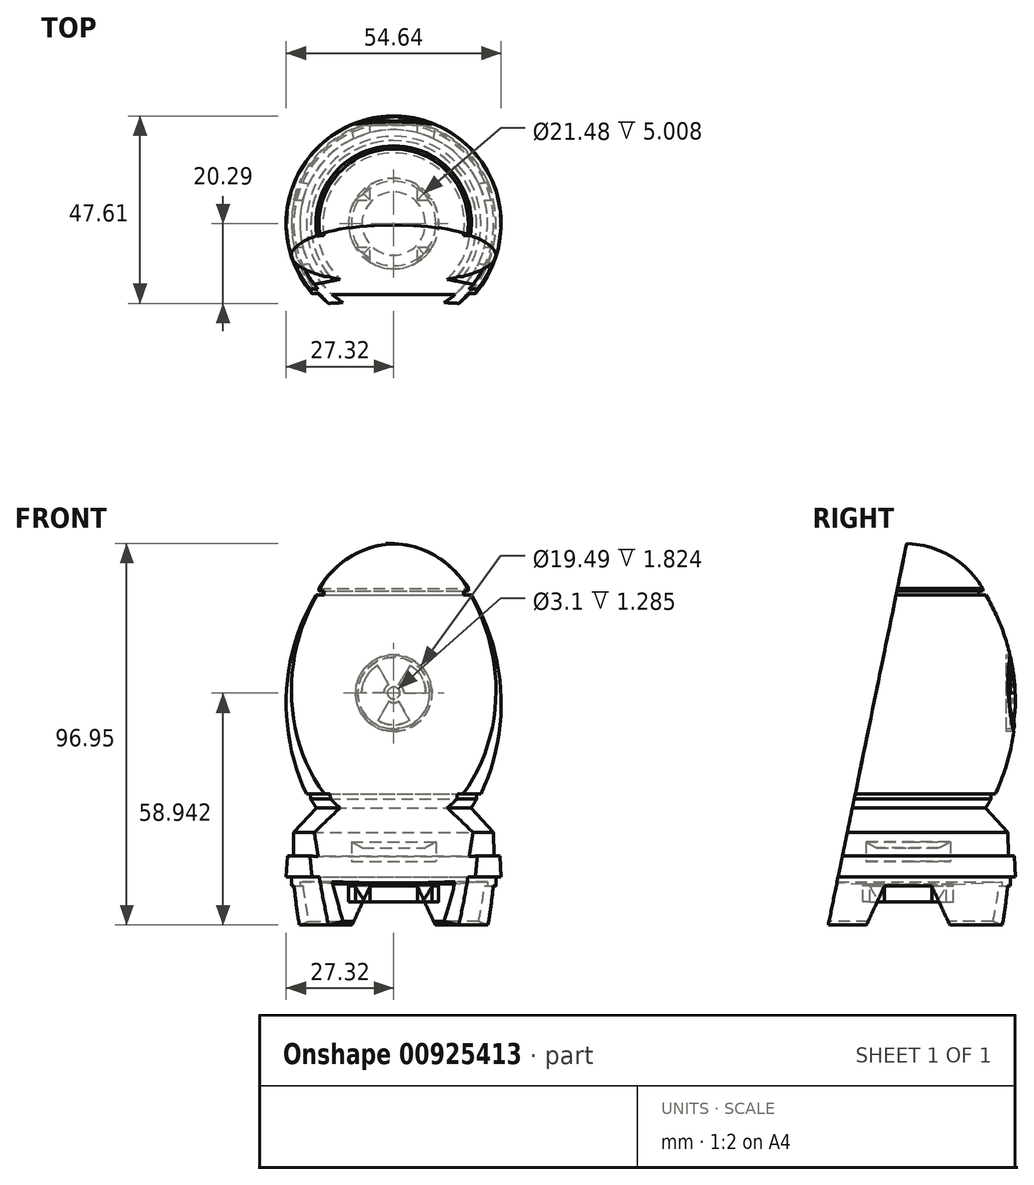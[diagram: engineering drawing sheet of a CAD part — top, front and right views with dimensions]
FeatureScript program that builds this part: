
annotation { "Feature Type Name" : "Feature", "Feature Type Description" : "" }
export const myFeature = defineFeature(function(context is Context, id is Id, definition is map)
    precondition{}
    {
        {
            var Q0;
            Q0=qCreatedBy(makeId("Front.planeOp"),FACE);
            var sketch = newSketch(context, id + "F0", { "sketchPlane" : qUnion([Q0])});
            skLineSegment(sketch, "E0", {"start": v(0, 0) * mm, "end": v(0, 100) * mm, "construction": true});
            skArc(sketch, "E1", {"start": v(18.96, 88.63) * mm, "mid": v(10.92, 96.72) * mm, "end": v(0, 100) * mm});
            skLineSegment(sketch, "E2", {"start": v(18.96, 88.63) * mm, "end": v(18.96, 87.9) * mm});
            skLineSegment(sketch, "E3", {"start": v(18.96, 87.9) * mm, "end": v(17.96, 87.9) * mm});
            skLineSegment(sketch, "E4", {"start": v(17.96, 87.9) * mm, "end": v(17.96, 86.91) * mm});
            skLineSegment(sketch, "E5", {"start": v(17.96, 86.91) * mm, "end": v(19.76, 86.91) * mm});
            skArc(sketch, "E6", {"start": v(22.17, 36.4) * mm, "mid": v(27.23, 61.96) * mm, "end": v(19.76, 86.91) * mm});
            skLineSegment(sketch, "E7", {"start": v(22.17, 36.4) * mm, "end": v(21.07, 36.4) * mm});
            skLineSegment(sketch, "E8", {"start": v(21.07, 36.4) * mm, "end": v(21.07, 35.46) * mm});
            skLineSegment(sketch, "E9", {"start": v(21.07, 35.46) * mm, "end": v(21.07, 35.1) * mm});
            skLineSegment(sketch, "E10", {"start": v(0, 35.1) * mm, "end": v(0, 100) * mm});
            skLineSegment(sketch, "E11", {"start": v(0, 100) * mm, "end": v(0, 35.1) * mm});
            skArc(sketch, "E12", {"start": v(8.03, 22.68) * mm, "mid": v(9.4, 23.43) * mm, "end": v(10.74, 24.24) * mm});
            skLineSegment(sketch, "E13", {"start": v(8.03, 22.68) * mm, "end": v(0, 22.68) * mm});
            skLineSegment(sketch, "E14", {"start": v(0, 22.68) * mm, "end": v(0, 35.1) * mm});
            skLineSegment(sketch, "E15", {"start": v(19.63, 32.82) * mm, "end": v(25.4, 26.58) * mm});
            skLineSegment(sketch, "E16", {"start": v(25.4, 26.58) * mm, "end": v(25.44, 20.54) * mm});
            skLineSegment(sketch, "E17", {"start": v(25.44, 20.54) * mm, "end": v(27.02, 20.6) * mm});
            skLineSegment(sketch, "E18", {"start": v(27.02, 20.6) * mm, "end": v(27.32, 15.33) * mm});
            skLineSegment(sketch, "E19", {"start": v(27.32, 15.33) * mm, "end": v(25.94, 15.26) * mm});
            skLineSegment(sketch, "E20", {"start": v(25.94, 15.26) * mm, "end": v(26.17, 3.07) * mm});
            skLineSegment(sketch, "E21", {"start": v(26.17, 3.07) * mm, "end": v(23.84, 4.04) * mm});
            skLineSegment(sketch, "E22", {"start": v(23.84, 4.04) * mm, "end": v(23.84, 14.09) * mm});
            skLineSegment(sketch, "E23", {"start": v(23.84, 14.09) * mm, "end": v(11.52, 13.35) * mm});
            skLineSegment(sketch, "E24", {"start": v(11.52, 13.35) * mm, "end": v(9.23, 1.76) * mm});
            skLineSegment(sketch, "E25", {"start": v(9.23, 1.76) * mm, "end": v(0, 1.76) * mm});
            skLineSegment(sketch, "E26", {"start": v(0, 1.76) * mm, "end": v(0, 22.68) * mm});
            skLineSegment(sketch, "E27", {"start": v(10.74, 24.24) * mm, "end": v(10.74, 19.23) * mm});
            skLineSegment(sketch, "E28", {"start": v(10.74, 19.23) * mm, "end": v(0, 19.23) * mm});
            skLineSegment(sketch, "E29", {"start": v(0, 19.23) * mm, "end": v(0, 22.68) * mm});
            skArc(sketch, "E30.trimOffspring", {"start": v(19.63, 32.82) * mm, "mid": v(20.38, 33.95) * mm, "end": v(21.07, 35.1) * mm});
            skSolve(sketch);
        }
        {
            var Q0;
            Q0=makeQuery(id+"F0.imprint","IMPRINT",FACE,{"disambiguationData":[TD([[makeQuery(id+"F0.imprint","IMPRINT",EDGE,{"derivedFrom":sQuery(id+"F0.wireOp",EDGE,"E1")}),1.0]])]});
            var Q1;
            Q1=sQuery(id+"F0.wireOp",EDGE,"E10");
            revolve(context, id + "F1", {"surfaceOperationType" : NewSurfaceOperationType.NEW, "entities" : qUnion([Q0]), "axis" : qUnion([Q1]), "revolveType" : RevolveType.FULL});
        }
        {
            var Q0;
            Q0=qCreatedBy(makeId("Right.planeOp"),FACE);
            var sketch = newSketch(context, id + "F2", { "sketchPlane" : qUnion([Q0])});
            skPoint(sketch, "E31.start.orphan", {"position": v(0, 13) * mm});
            skLineSegment(sketch, "E32", {"start": v(0, 0) * mm, "end": v(12, 0) * mm});
            skLineSegment(sketch, "E33", {"start": v(0, 0) * mm, "end": v(-12, 0) * mm});
            skLineSegment(sketch, "E34", {"start": v(0, 0) * mm, "end": v(0, 13) * mm, "construction": true});
            skLineSegment(sketch, "E35", {"start": v(0, 13) * mm, "end": v(6, 13) * mm});
            skLineSegment(sketch, "E36", {"start": v(0, 13) * mm, "end": v(-6, 13) * mm});
            skLineSegment(sketch, "E37", {"start": v(-6, 13) * mm, "end": v(-12, 0) * mm});
            skLineSegment(sketch, "E38", {"start": v(6, 13) * mm, "end": v(12, 0) * mm});
            skSolve(sketch);
        }
        {
            var Q0;
            Q0=makeQuery(id+"F2.imprint","IMPRINT",FACE,{"disambiguationData":[TD([[makeQuery(id+"F2.imprint","IMPRINT",EDGE,{"derivedFrom":sQuery(id+"F2.wireOp",EDGE,"E32")}),1.0]])]});
            extrude(context, id + "F3", {"entities" : qUnion([Q0]), "operationType" : NewBodyOperationType.REMOVE, "endBound" : BoundingType.SYMMETRIC, "oppositeDirection" : true, "depth" : 70 * mm, "offsetDistance" : 25 * mm});
        }
        {
            var Q0;
            Q0=qCreatedBy(makeId("Front.planeOp"),FACE);
            var sketch = newSketch(context, id + "F4", { "sketchPlane" : qUnion([Q0])});
            skLineSegment(sketch, "E39", {"start": v(0, 0) * mm, "end": v(12, 0) * mm});
            skLineSegment(sketch, "E40", {"start": v(0, 0) * mm, "end": v(-12, 0) * mm});
            skLineSegment(sketch, "E41", {"start": v(0, 0) * mm, "end": v(0, 13) * mm, "construction": true});
            skLineSegment(sketch, "E42", {"start": v(0, 13) * mm, "end": v(6, 13) * mm});
            skLineSegment(sketch, "E43", {"start": v(0, 13) * mm, "end": v(-6, 13) * mm});
            skLineSegment(sketch, "E44", {"start": v(-6, 13) * mm, "end": v(-12, 0) * mm});
            skLineSegment(sketch, "E45", {"start": v(6, 13) * mm, "end": v(12, 0) * mm});
            skSolve(sketch);
        }
        {
            var Q0;
            Q0=makeQuery(id+"F4.imprint","IMPRINT",FACE,{"disambiguationData":[TD([[makeQuery(id+"F4.imprint","IMPRINT",EDGE,{"derivedFrom":sQuery(id+"F4.wireOp",EDGE,"E39")}),1.0]])]});
            extrude(context, id + "F5", {"entities" : qUnion([Q0]), "operationType" : NewBodyOperationType.REMOVE, "endBound" : BoundingType.SYMMETRIC, "depth" : 70 * mm, "offsetDistance" : 25 * mm});
        }
        {
            var Q0;
            Q0=makeQuery(id+"F5.boolean.opBoolean","MERGE",FACE,{"derivedFrom":[makeQuery(id+"F3.boolean.opBoolean","COPY",FACE,{"disambiguationData":[TD([makeQuery(id+"F1.opRevolve","SWEPT_FACE",FACE,{"disambiguationData":[OSD([sQuery(id+"F0.wireOp",EDGE,"E24")])]}),makeQuery(id+"F3.opExtrude","SWEPT_FACE",FACE,{"disambiguationData":[OSD([sQuery(id+"F2.wireOp",EDGE,"E37")])]}),makeQuery(id+"F3.opExtrude","SWEPT_FACE",FACE,{"disambiguationData":[OSD([sQuery(id+"F2.wireOp",EDGE,"E38")])]})])],"derivedFrom":makeQuery(id+"F3.opExtrude","SWEPT_FACE",FACE,{"disambiguationData":[OSD([sQuery(id+"F2.wireOp",EDGE,"E35"),sQuery(id+"F2.wireOp",EDGE,"E36")])]})})],"fromTools":[makeQuery(id+"F5.opExtrude","SWEPT_FACE",FACE,{"disambiguationData":[OSD([sQuery(id+"F4.wireOp",EDGE,"E42"),sQuery(id+"F4.wireOp",EDGE,"E43")])]})]});
            extrude(context, id + "F6", {"entities" : qUnion([Q0]), "operationType" : NewBodyOperationType.ADD, "depth" : 4 * mm, "offsetDistance" : 25 * mm});
        }
        {
            var Q0;
            Q0=qCreatedBy(makeId("Right.planeOp"),FACE);
            var sketch = newSketch(context, id + "F7", { "sketchPlane" : qUnion([Q0])});
            skLineSegment(sketch, "E46", {"start": v(0, 0) * mm, "end": v(-41.84, 0) * mm});
            skLineSegment(sketch, "E47", {"start": v(-41.84, 0) * mm, "end": v(-41.84, 98.88) * mm});
            skLineSegment(sketch, "E48", {"start": v(-41.84, 98.88) * mm, "end": v(-41.84, 101.8) * mm});
            skLineSegment(sketch, "E49", {"start": v(-41.84, 101.8) * mm, "end": v(0, 101.8) * mm});
            skLineSegment(sketch, "E50", {"start": v(0, 101.8) * mm, "end": v(35.34, 101.8) * mm});
            skLineSegment(sketch, "E51", {"start": v(35.34, 101.8) * mm, "end": v(35.34, 0) * mm});
            skLineSegment(sketch, "E52", {"start": v(35.34, 0) * mm, "end": v(0, 0) * mm});
            skLineSegment(sketch, "E53", {"start": v(0, 101.8) * mm, "end": v(-20.92, 0) * mm});
            skLineSegment(sketch, "E54", {"start": v(35.34, 101.8) * mm, "end": v(-20.92, 0) * mm});
            skSolve(sketch);
        }
        {
            var Q0;
            {var subQ0=sQuery(id+"F7.wireOp",EDGE,"E47");Q0=makeQuery(id+"F7.imprint","IMPRINT",FACE,{"disambiguationData":[TD([[makeQuery(id+"F7.imprint","IMPRINT",EDGE,{"derivedFrom":subQ0}),-1.0]])]});}
            extrude(context, id + "F8", {"entities" : qUnion([Q0]), "operationType" : NewBodyOperationType.REMOVE, "endBound" : BoundingType.SYMMETRIC, "oppositeDirection" : true, "depth" : 100 * mm, "offsetDistance" : 25 * mm});
        }
        {
            var Q0;
            Q0=qCreatedBy(makeId("Front.planeOp"),FACE);
            var sketch = newSketch(context, id + "F9", { "sketchPlane" : qUnion([Q0])});
            skCircle(sketch, "E55", {"center": v(0, 62.01) * mm, "radius": 1.55 * mm});
            skCircle(sketch, "E56", {"center": v(0, 62.01) * mm, "radius": 9.14 * mm});
            skLineSegment(sketch, "E57", {"start": v(2.62, 62.07) * mm, "end": v(8.08, 62.07) * mm});
            skArc(sketch, "E58", {"start": v(8.08, 62.07) * mm, "mid": v(7.13, 66.14) * mm, "end": v(4.1, 69.01) * mm});
            skLineSegment(sketch, "E59", {"start": v(4.1, 69.01) * mm, "end": v(1.27, 64.21) * mm});
            skArc(sketch, "E60", {"start": v(2.62, 62.07) * mm, "mid": v(2.19, 63.3) * mm, "end": v(1.27, 64.21) * mm});
            skLineSegment(sketch, "E61", {"start": v(-1.26, 64.2) * mm, "end": v(-4.08, 69.08) * mm});
            skLineSegment(sketch, "E62", {"start": v(-2.42, 62.04) * mm, "end": v(-8.15, 62.04) * mm});
            skLineSegment(sketch, "E63", {"start": v(-1.2, 59.95) * mm, "end": v(-3.97, 55.07) * mm});
            skLineSegment(sketch, "E64", {"start": v(1.2, 59.9) * mm, "end": v(4, 55.1) * mm});
            skArc(sketch, "E65", {"start": v(-3.97, 55.07) * mm, "mid": v(0.02, 53.92) * mm, "end": v(4, 55.1) * mm});
            skArc(sketch, "E66", {"start": v(-1.2, 59.95) * mm, "mid": v(-0.01, 59.5) * mm, "end": v(1.2, 59.9) * mm});
            skArc(sketch, "E67", {"start": v(-1.26, 64.2) * mm, "mid": v(-2.16, 63.3) * mm, "end": v(-2.42, 62.04) * mm});
            skArc(sketch, "E68", {"start": v(-4.08, 69.08) * mm, "mid": v(-7, 66.08) * mm, "end": v(-8.15, 62.04) * mm});
            skCircle(sketch, "E69", {"center": v(0, 62.01) * mm, "radius": 1.56 * mm});
            skCircle(sketch, "E70", {"center": v(0, 62.01) * mm, "radius": 9.75 * mm});
            skSolve(sketch);
        }
        {
            var Q0;
            Q0=makeQuery(id+"F9.imprint","IMPRINT",FACE,{"disambiguationData":[TD([[makeQuery(id+"F9.imprint","IMPRINT",EDGE,{"derivedFrom":sQuery(id+"F9.wireOp",EDGE,"E61")}),1.0]])]});
            var Q1;
            Q1=makeQuery(id+"F9.imprint","IMPRINT",FACE,{"disambiguationData":[TD([[makeQuery(id+"F9.imprint","IMPRINT",EDGE,{"derivedFrom":sQuery(id+"F9.wireOp",EDGE,"E57")}),1.0]])]});
            var Q2;
            Q2=makeQuery(id+"F9.imprint","IMPRINT",FACE,{"disambiguationData":[TD([[makeQuery(id+"F9.imprint","IMPRINT",EDGE,{"derivedFrom":sQuery(id+"F9.wireOp",EDGE,"E55")}),1.0]])]});
            var Q3;
            Q3=makeQuery(id+"F9.imprint","IMPRINT",FACE,{"disambiguationData":[TD([[makeQuery(id+"F9.imprint","IMPRINT",EDGE,{"derivedFrom":sQuery(id+"F9.wireOp",EDGE,"E63")}),1.0]])]});
            var Q4;
            Q4=makeQuery(id+"F9.imprint","IMPRINT",FACE,{"disambiguationData":[TD([[makeQuery(id+"F9.imprint","IMPRINT",EDGE,{"derivedFrom":sQuery(id+"F9.wireOp",EDGE,"E56")}),-1.0]])]});
            extrude(context, id + "F10", {"entities" : qUnion([Q0, Q1, Q2, Q3, Q4]), "operationType" : NewBodyOperationType.REMOVE, "oppositeDirection" : true, "depth" : 31.6 * mm, "offsetDistance" : 25 * mm});
        }
        {
            var Q0;
            Q0=makeQuery(id+"F10.boolean.opBoolean","COPY",FACE,{"derivedFrom":makeQuery(id+"F10.opExtrude","CAP_FACE",FACE,{"disambiguationData":[OSD([sQuery(id+"F9.wireOp",EDGE,"E57"),sQuery(id+"F9.wireOp",EDGE,"E58"),sQuery(id+"F9.wireOp",EDGE,"E59"),sQuery(id+"F9.wireOp",EDGE,"E60")])],"isStart":true})});
            var Q1;
            Q1=makeQuery(id+"F10.boolean.opBoolean","COPY",FACE,{"derivedFrom":makeQuery(id+"F10.opExtrude","CAP_FACE",FACE,{"disambiguationData":[OSD([sQuery(id+"F9.wireOp",EDGE,"E61"),sQuery(id+"F9.wireOp",EDGE,"E62"),sQuery(id+"F9.wireOp",EDGE,"E67"),sQuery(id+"F9.wireOp",EDGE,"E68")])],"isStart":true})});
            var Q2;
            Q2=makeQuery(id+"F10.boolean.opBoolean","COPY",FACE,{"derivedFrom":makeQuery(id+"F10.opExtrude","CAP_FACE",FACE,{"disambiguationData":[OSD([sQuery(id+"F9.wireOp",EDGE,"E63"),sQuery(id+"F9.wireOp",EDGE,"E64"),sQuery(id+"F9.wireOp",EDGE,"E65"),sQuery(id+"F9.wireOp",EDGE,"E66")])],"isStart":true})});
            var Q3;
            Q3=makeQuery(id+"F10.boolean.opBoolean","COPY",FACE,{"derivedFrom":makeQuery(id+"F10.opExtrude","CAP_FACE",FACE,{"disambiguationData":[OSD([sQuery(id+"F9.wireOp",EDGE,"E56"),sQuery(id+"F9.wireOp",EDGE,"E70")])],"isStart":true})});
            var Q4;
            Q4=makeQuery(id+"F10.boolean.opBoolean","COPY",FACE,{"derivedFrom":makeQuery(id+"F10.opExtrude","CAP_FACE",FACE,{"disambiguationData":[OSD([sQuery(id+"F9.wireOp",EDGE,"E55")])],"isStart":true})});
            extrude(context, id + "F11", {"entities" : qUnion([Q0, Q1, Q2, Q3, Q4]), "operationType" : NewBodyOperationType.ADD, "depth" : 26 * mm, "offsetDistance" : 25 * mm});
        }
        {
            var Q0;
            Q0=makeQuery(id+"F11.opExtrude","CAP_FACE",FACE,{"disambiguationData":[OSD([sQuery(id+"F9.wireOp",EDGE,"E56"),sQuery(id+"F9.wireOp",EDGE,"E70")])],"isStart":false});
            extrude(context, id + "F12", {"entities" : qUnion([Q0]), "operationType" : NewBodyOperationType.REMOVE, "oppositeDirection" : true, "depth" : 1 * mm, "offsetDistance" : 25 * mm});
        }
    });
